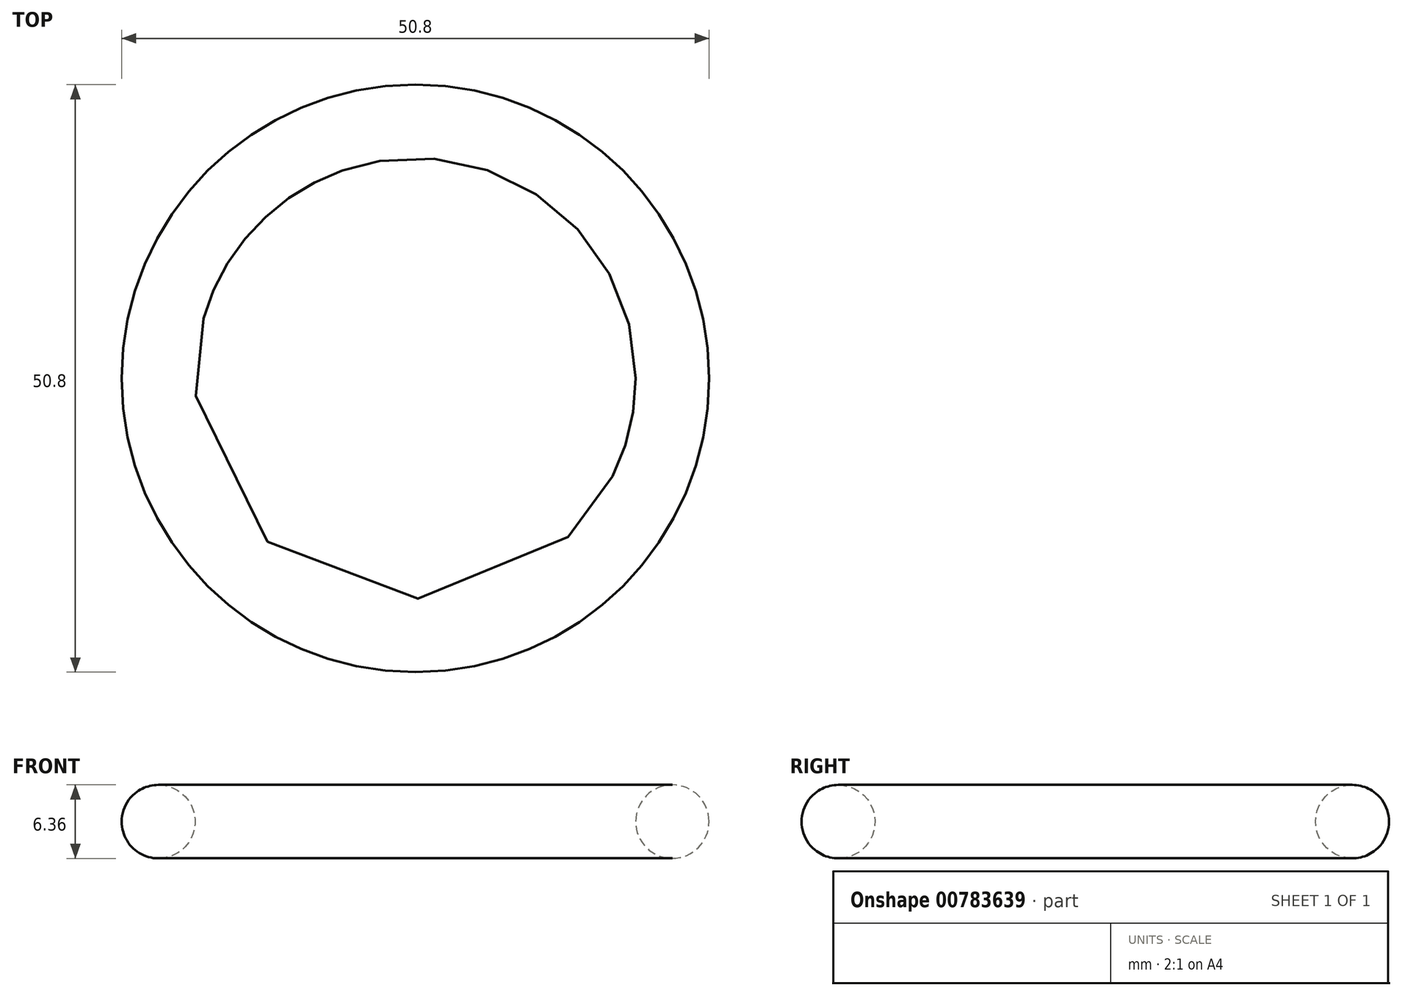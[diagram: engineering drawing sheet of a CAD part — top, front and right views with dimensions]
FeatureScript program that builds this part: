
annotation { "Feature Type Name" : "Feature", "Feature Type Description" : "" }
export const myFeature = defineFeature(function(context is Context, id is Id, definition is map)
    precondition{}
    {
        {
            var Q0;
            Q0=qCreatedBy(makeId("Right.planeOp"),FACE);
            var sketch = newSketch(context, id + "F0", { "sketchPlane" : qUnion([Q0])});
            skCircle(sketch, "E0", {"center": v(-22.22, 0) * mm, "radius": 3.18 * mm});
            skLineSegment(sketch, "E1", {"start": v(0, 16.12) * mm, "end": v(0, -14.1) * mm, "construction": true});
            skSolve(sketch);
        }
        {
            var Q0;
            Q0 = qSketchRegion(id + "F0", true);
            var Q1;
            Q1=sQuery(id+"F0.wireOp",EDGE,"E1");
            revolve(context, id + "F1", {"surfaceOperationType" : NewSurfaceOperationType.NEW, "entities" : qUnion([Q0]), "axis" : qUnion([Q1]), "revolveType" : RevolveType.FULL});
        }
    });
